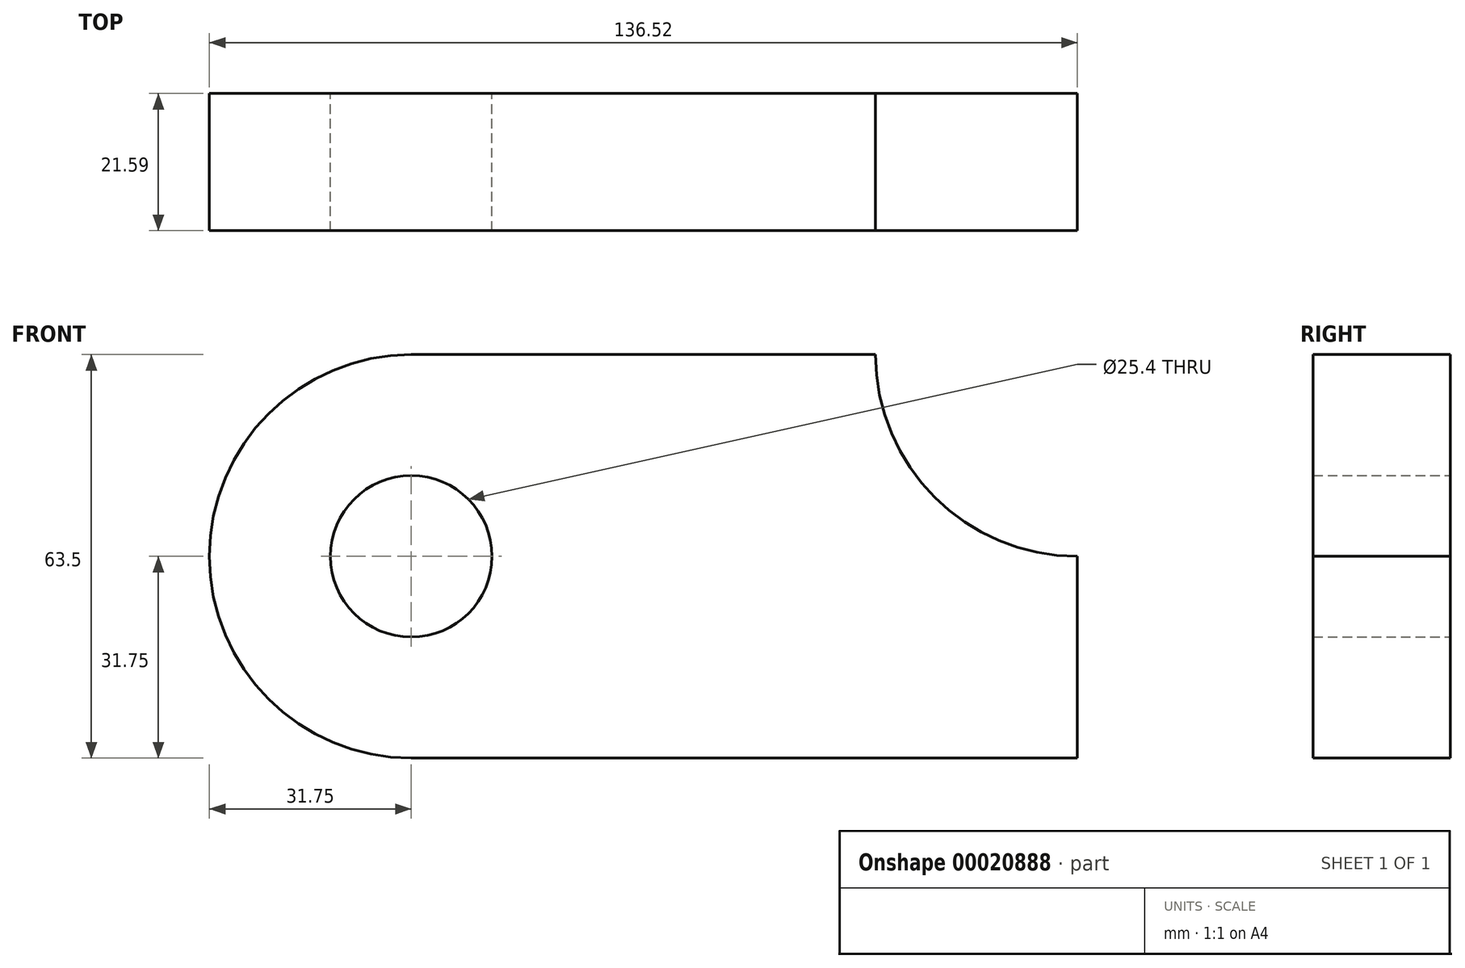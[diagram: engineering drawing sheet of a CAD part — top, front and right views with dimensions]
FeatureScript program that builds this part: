
annotation { "Feature Type Name" : "Feature", "Feature Type Description" : "" }
export const myFeature = defineFeature(function(context is Context, id is Id, definition is map)
    precondition{}
    {
        {
            var Q0;
            Q0=qCreatedBy(makeId("Front.planeOp"),FACE);
            var sketch = newSketch(context, id + "F0", { "sketchPlane" : qUnion([Q0])});
            skLineSegment(sketch, "E0.bottom", {"start": v(0, 0) * mm, "end": v(104.78, 0) * mm});
            skLineSegment(sketch, "E0.top", {"start": v(0, 63.5) * mm, "end": v(73.02, 63.5) * mm});
            skLineSegment(sketch, "E0.left", {"start": v(0, 0) * mm, "end": v(0, 63.5) * mm});
            skLineSegment(sketch, "E0.right", {"start": v(104.78, 0) * mm, "end": v(104.78, 31.75) * mm});
            skCircle(sketch, "E1", {"center": v(0, 31.75) * mm, "radius": 31.75 * mm});
            skCircle(sketch, "E2", {"center": v(0, 31.75) * mm, "radius": 12.7 * mm});
            skArc(sketch, "E3", {"start": v(73.02, 63.5) * mm, "mid": v(82.32, 41.05) * mm, "end": v(104.77, 31.75) * mm});
            skSolve(sketch);
        }
        {
            var Q0;
            {var subQ3=sQuery(id+"F0.wireOp",EDGE,"E0.bottom");Q0=makeQuery(id+"F0.imprint","IMPRINT",FACE,{"disambiguationData":[TD([[makeQuery(id+"F0.imprint","IMPRINT",EDGE,{"derivedFrom":subQ3}),1.0]])]});}
            var Q1;
            {var subQ0=sQuery(id+"F0.wireOp",EDGE,"E2");var subQ1=sQuery(id+"F0.wireOp",EDGE,"E0.left");var subQ3=makeQuery(id+"F0.imprint","INTERSECT",VERTEX,{"disambiguationData":[OD(0.0)],"derivedFrom":[subQ1,subQ0]});Q1=makeQuery(id+"F0.imprint","IMPRINT",FACE,{"disambiguationData":[TD([[makeQuery(id+"F0.imprint","IMPRINT",EDGE,{"disambiguationData":[TD([[subQ3,-1.0]])],"derivedFrom":subQ0}),-1.0]])]});}
            var Q2;
            {var subQ0=sQuery(id+"F0.wireOp",EDGE,"E2");var subQ1=sQuery(id+"F0.wireOp",EDGE,"E0.left");var subQ3=makeQuery(id+"F0.imprint","INTERSECT",VERTEX,{"disambiguationData":[OD(0.0)],"derivedFrom":[subQ1,subQ0]});Q2=makeQuery(id+"F0.imprint","IMPRINT",FACE,{"disambiguationData":[TD([[makeQuery(id+"F0.imprint","IMPRINT",EDGE,{"disambiguationData":[TD([[subQ3,1.0]])],"derivedFrom":subQ0}),-1.0]])]});}
            extrude(context, id + "F1", {"entities" : qUnion([Q0, Q1, Q2]), "depth" : 21.59 * mm});
        }
    });
